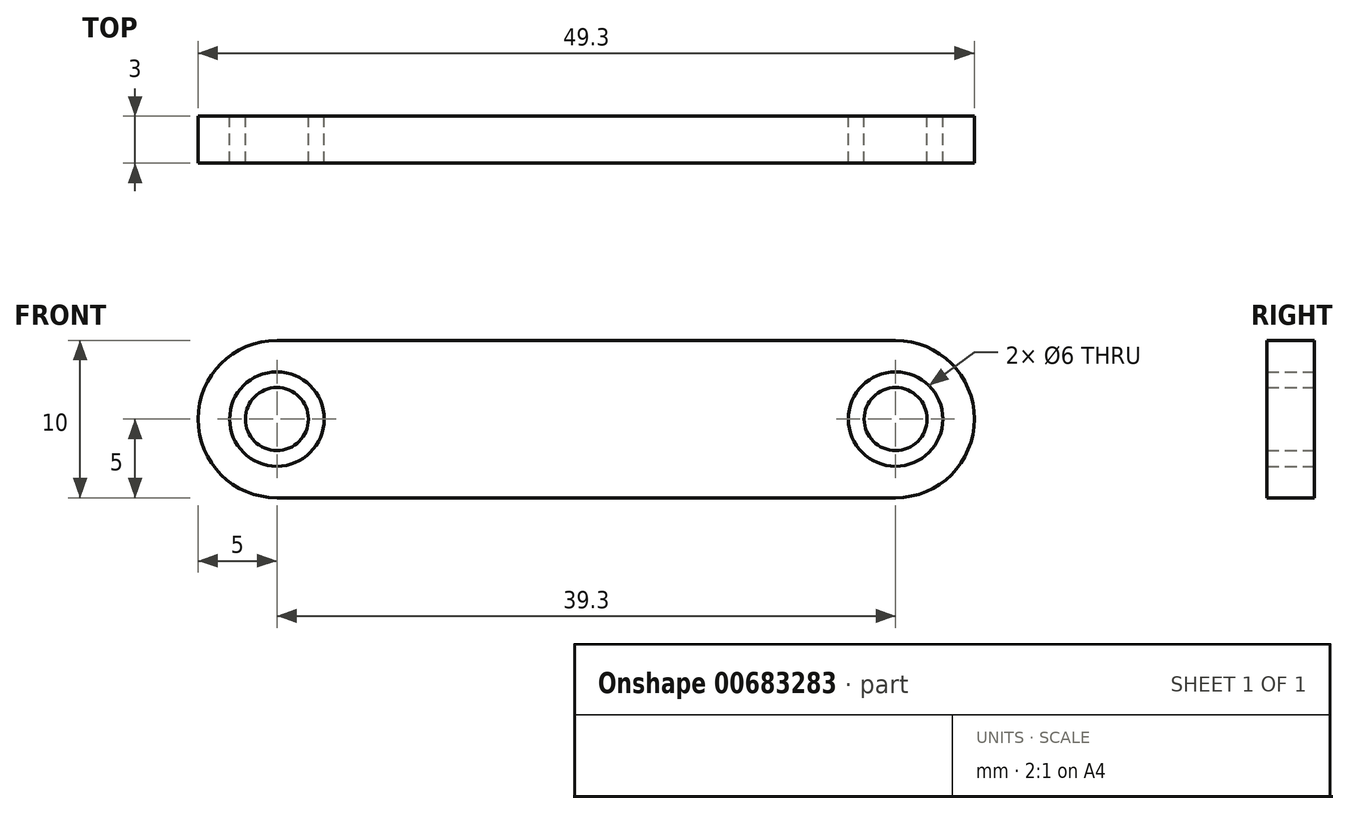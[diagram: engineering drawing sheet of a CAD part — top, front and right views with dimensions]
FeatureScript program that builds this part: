
annotation { "Feature Type Name" : "Feature", "Feature Type Description" : "" }
export const myFeature = defineFeature(function(context is Context, id is Id, definition is map)
    precondition{}
    {
        {
            var Q0;
            Q0=qCreatedBy(makeId("Front.planeOp"),FACE);
            var sketch = newSketch(context, id + "F0", { "sketchPlane" : qUnion([Q0])});
            skArc(sketch, "E0", {"start": v(-19.65, 5) * mm, "mid": v(-24.65, 0) * mm, "end": v(-19.65, -5) * mm});
            skArc(sketch, "E1", {"start": v(19.65, -5) * mm, "mid": v(24.65, 0) * mm, "end": v(19.65, 5) * mm});
            skLineSegment(sketch, "E2", {"start": v(-19.65, 5) * mm, "end": v(19.65, 5) * mm});
            skLineSegment(sketch, "E3", {"start": v(-19.65, -5) * mm, "end": v(19.65, -5) * mm});
            skCircle(sketch, "E4", {"center": v(-19.65, 0) * mm, "radius": 3 * mm});
            skCircle(sketch, "E5", {"center": v(-19.65, 0) * mm, "radius": 2 * mm});
            skCircle(sketch, "E6", {"center": v(19.65, 0) * mm, "radius": 3 * mm});
            skCircle(sketch, "E7", {"center": v(19.65, 0) * mm, "radius": 2 * mm});
            skSolve(sketch);
        }
        {
            var Q0;
            Q0 = qSketchRegion(id + "F0", true);
            var Q1;
            Q1=makeQuery(id+"F0.imprint","IMPRINT",FACE,{"disambiguationData":[TD([[makeQuery(id+"F0.imprint","IMPRINT",EDGE,{"derivedFrom":sQuery(id+"F0.wireOp",EDGE,"E5")}),1.0]])]});
            var Q2;
            Q2=makeQuery(id+"F0.imprint","IMPRINT",FACE,{"disambiguationData":[TD([[makeQuery(id+"F0.imprint","IMPRINT",EDGE,{"derivedFrom":sQuery(id+"F0.wireOp",EDGE,"E7")}),1.0]])]});
            extrude(context, id + "F1", {"entities" : qUnion([Q0, Q1, Q2]), "depth" : 3 * mm, "offsetDistance" : 25 * mm});
        }
    });
